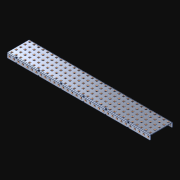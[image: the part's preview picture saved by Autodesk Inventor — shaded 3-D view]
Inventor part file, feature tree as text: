
AUTODESK INVENTOR PART (.ipt)
format: ipt  version: 2021 (Build 250183000, 183)  size: 2,406,400 bytes
history: native  units: in
note: dims shown in document units (in); Inventor stores cm internally (conversion verified against a paired STEP export)
features: extrude x225, other x225, sketch x4, pattern_linear x3
ambient origin geometry x8: Origin, YZ Plane, XZ Plane, XY Plane, X Axis, Y Axis, Z Axis, Center Point
bodies: Solid1 (feature_tree)
feature tree (457):
  pattern_linear  "Rectangular Pattern1"  Spacing1=0.182in  [1 undecoded]
  pattern_linear  "Rectangular Pattern2"  Spacing1=0.046in  [1 undecoded]
  pattern_linear  "Rectangular Pattern3"  Spacing1=0.5in  [1 undecoded]
  extrude  "Extrusion1"  Depth=0.046in
  sketch  "Sketch1"  dims[d0=0.182in]
  other  "Srf1"
  sketch  "Sketch2"  dims[d1=0.046in d2=0.0in]
  other  "Srf2"
  sketch  "Sketch3"  dims[d3=0.182in]
  other  "Srf3"
  other  "Srf4"
  other  "Srf5"
  other  "Srf6"
  other  "Srf7"
  other  "Srf8"
  other  "Srf9"
  other  "Srf10"
  other  "Srf11"
  other  "Srf12"
  other  "Srf13"
  other  "Srf14"
  other  "Srf15"
  other  "Srf16"
  other  "Srf17"
  other  "Srf18"
  other  "Srf19"
  other  "Srf20"
  other  "Srf21"
  other  "Srf22"
  other  "Srf23"
  other  "Srf24"
  other  "Srf25"
  other  "Srf26"
  other  "Srf27"
  other  "Srf28"
  other  "Srf29"
  other  "Srf30"
  other  "Srf31"
  other  "Srf32"
  other  "Srf33"
  other  "Srf34"
  other  "Srf38"
  other  "Srf39"
  other  "Srf40"
  other  "Srf41"
  other  "Srf42"
  other  "Srf43"
  other  "Srf44"
  other  "Srf45"
  other  "Srf46"
  other  "Srf47"
  other  "Srf48"
  other  "Srf49"
  other  "Srf50"
  other  "Srf51"
  other  "Srf52"
  other  "Srf53"
  other  "Srf54"
  other  "Srf55"
  other  "Srf56"
  other  "Srf57"
  other  "Srf58"
  other  "Srf59"
  other  "Srf60"
  other  "Srf61"
  other  "Srf62"
  other  "Srf63"
  other  "Srf64"
  other  "Srf65"
  other  "Srf66"
  other  "Srf67"
  other  "Srf68"
  other  "Srf72"
  other  "Srf73"
  other  "Srf74"
  other  "Srf75"
  other  "Srf76"
  other  "Srf77"
  other  "Srf78"
  other  "Srf79"
  other  "Srf80"
  other  "Srf81"
  other  "Srf82"
  other  "Srf83"
  other  "Srf84"
  other  "Srf85"
  other  "Srf86"
  other  "Srf87"
  other  "Srf88"
  other  "Srf89"
  other  "Srf90"
  other  "Srf91"
  other  "Srf92"
  other  "Srf93"
  other  "Srf94"
  other  "Srf95"
  other  "Srf96"
  other  "Srf97"
  other  "Srf98"
  other  "Srf99"
  other  "Srf100"
  other  "Srf101"
  other  "Srf102"
  other  "Srf103"
  other  "Srf107"
  other  "Srf108"
  other  "Srf109"
  other  "Srf110"
  other  "Srf111"
  other  "Srf112"
  other  "Srf113"
  other  "Srf114"
  other  "Srf115"
  other  "Srf116"
  other  "Srf117"
  other  "Srf118"
  other  "Srf119"
  other  "Srf120"
  other  "Srf121"
  other  "Srf122"
  other  "Srf123"
  other  "Srf124"
  other  "Srf125"
  other  "Srf126"
  other  "Srf127"
  other  "Srf128"
  other  "Srf129"
  other  "Srf130"
  other  "Srf131"
  other  "Srf132"
  other  "Srf133"
  other  "Srf134"
  other  "Srf135"
  other  "Srf136"
  other  "Srf137"
  other  "Srf138"
  other  "Srf142"
  other  "Srf143"
  other  "Srf144"
  other  "Srf145"
  other  "Srf146"
  other  "Srf147"
  other  "Srf148"
  other  "Srf149"
  other  "Srf150"
  other  "Srf151"
  other  "Srf152"
  other  "Srf153"
  other  "Srf154"
  other  "Srf155"
  other  "Srf156"
  other  "Srf157"
  other  "Srf158"
  other  "Srf159"
  other  "Srf160"
  other  "Srf161"
  other  "Srf162"
  other  "Srf163"
  other  "Srf164"
  other  "Srf165"
  other  "Srf166"
  other  "Srf167"
  other  "Srf168"
  other  "Srf169"
  other  "Srf170"
  other  "Srf171"
  other  "Srf172"
  other  "Srf173"
  other  "Srf177"
  other  "Srf178"
  other  "Srf179"
  other  "Srf180"
  other  "Srf181"
  other  "Srf182"
  other  "Srf183"
  other  "Srf184"
  other  "Srf185"
  other  "Srf186"
  other  "Srf187"
  other  "Srf188"
  other  "Srf189"
  other  "Srf190"
  other  "Srf191"
  other  "Srf192"
  other  "Srf193"
  other  "Srf194"
  other  "Srf195"
  other  "Srf196"
  other  "Srf197"
  other  "Srf198"
  other  "Srf199"
  other  "Srf200"
  other  "Srf201"
  other  "Srf202"
  other  "Srf203"
  other  "Srf204"
  other  "Srf205"
  other  "Srf206"
  other  "Srf207"
  other  "Srf208"
  other  "Srf212"
  other  "Srf213"
  other  "Srf214"
  other  "Srf215"
  other  "Srf216"
  other  "Srf217"
  other  "Srf218"
  other  "Srf219"
  other  "Srf220"
  other  "Srf221"
  other  "Srf222"
  other  "Srf223"
  other  "Srf224"
  other  "Srf225"
  other  "Srf226"
  other  "Srf227"
  other  "Srf228"
  other  "Srf229"
  other  "Srf230"
  other  "Srf231"
  other  "Srf232"
  other  "Srf233"
  other  "Srf234"
  other  "Srf235"
  other  "Srf236"
  other  "Srf237"
  other  "Srf238"
  other  "Srf239"
  other  "Srf240"
  other  "Srf241"
  other  "Srf242"
  sketch  "Sketch4"  dims[d4=0.046in d5=0.0in d6=0.182in d7=0.046in d8=0.0in d11=0.5in d12=12.5984in d14=0.5in d15=1.9685in d17=0.5in d18=12.5984in d20=0.5in d21=1.5in d22=0.0in]
  parser-record x1  (decoder bookkeeping rows leaked as tree rows — omitted from the tree; the rows remain in map.json)
  extrude  "ExtrusionSrf1"  Depth=0.046in
  extrude  "ExtrusionSrf2"  Depth=0.046in
  extrude  "ExtrusionSrf3"  Depth=0.046in
  extrude  "ExtrusionSrf4"  Depth=0.046in
  extrude  "ExtrusionSrf5"  Depth=0.046in
  extrude  "ExtrusionSrf6"  TaperAngle=0.0deg  [1 undecoded]
  extrude  "ExtrusionSrf7"  [1 undecoded]
  extrude  "ExtrusionSrf8"  [1 undecoded]
  extrude  "ExtrusionSrf9"  [1 undecoded]
  extrude  "ExtrusionSrf10"  [1 undecoded]
  extrude  "ExtrusionSrf11"  [1 undecoded]
  extrude  "ExtrusionSrf12"  [1 undecoded]
  extrude  "ExtrusionSrf13"  [1 undecoded]
  extrude  "ExtrusionSrf14"  [1 undecoded]
  extrude  "ExtrusionSrf15"  [1 undecoded]
  extrude  "ExtrusionSrf16"  [1 undecoded]
  extrude  "ExtrusionSrf17"  [1 undecoded]
  extrude  "ExtrusionSrf18"  [1 undecoded]
  extrude  "ExtrusionSrf19"  [1 undecoded]
  extrude  "ExtrusionSrf20"  [1 undecoded]
  extrude  "ExtrusionSrf21"  [1 undecoded]
  extrude  "ExtrusionSrf22"  [1 undecoded]
  extrude  "ExtrusionSrf23"  [1 undecoded]
  extrude  "ExtrusionSrf24"  [1 undecoded]
  extrude  "ExtrusionSrf25"  [1 undecoded]
  extrude  "ExtrusionSrf26"  [1 undecoded]
  extrude  "ExtrusionSrf27"  [1 undecoded]
  extrude  "ExtrusionSrf28"  [1 undecoded]
  extrude  "ExtrusionSrf29"  [1 undecoded]
  extrude  "ExtrusionSrf30"  [1 undecoded]
  extrude  "ExtrusionSrf31"  [1 undecoded]
  extrude  "ExtrusionSrf32"  [1 undecoded]
  extrude  "ExtrusionSrf33"  [1 undecoded]
  extrude  "ExtrusionSrf34"  [1 undecoded]
  extrude  "ExtrusionSrf38"  [1 undecoded]
  extrude  "ExtrusionSrf39"  [1 undecoded]
  extrude  "ExtrusionSrf40"  [1 undecoded]
  extrude  "ExtrusionSrf41"  [1 undecoded]
  extrude  "ExtrusionSrf42"  [1 undecoded]
  extrude  "ExtrusionSrf43"  [1 undecoded]
  extrude  "ExtrusionSrf44"  [1 undecoded]
  extrude  "ExtrusionSrf45"  [1 undecoded]
  extrude  "ExtrusionSrf46"  [1 undecoded]
  extrude  "ExtrusionSrf47"  [1 undecoded]
  extrude  "ExtrusionSrf48"  [1 undecoded]
  extrude  "ExtrusionSrf49"  [1 undecoded]
  extrude  "ExtrusionSrf50"  [1 undecoded]
  extrude  "ExtrusionSrf51"  [1 undecoded]
  extrude  "ExtrusionSrf52"  [1 undecoded]
  extrude  "ExtrusionSrf53"  [1 undecoded]
  extrude  "ExtrusionSrf54"  [1 undecoded]
  extrude  "ExtrusionSrf55"  [1 undecoded]
  extrude  "ExtrusionSrf56"  [1 undecoded]
  extrude  "ExtrusionSrf57"  [1 undecoded]
  extrude  "ExtrusionSrf58"  [1 undecoded]
  extrude  "ExtrusionSrf59"  [1 undecoded]
  extrude  "ExtrusionSrf60"  [1 undecoded]
  extrude  "ExtrusionSrf61"  [1 undecoded]
  extrude  "ExtrusionSrf62"  [1 undecoded]
  extrude  "ExtrusionSrf63"  [1 undecoded]
  extrude  "ExtrusionSrf64"  [1 undecoded]
  extrude  "ExtrusionSrf65"  [1 undecoded]
  extrude  "ExtrusionSrf66"  [1 undecoded]
  extrude  "ExtrusionSrf67"  [1 undecoded]
  extrude  "ExtrusionSrf68"  [1 undecoded]
  extrude  "ExtrusionSrf72"  [1 undecoded]
  extrude  "ExtrusionSrf73"  [1 undecoded]
  extrude  "ExtrusionSrf74"  [1 undecoded]
  extrude  "ExtrusionSrf75"  [1 undecoded]
  extrude  "ExtrusionSrf76"  [1 undecoded]
  extrude  "ExtrusionSrf77"  [1 undecoded]
  extrude  "ExtrusionSrf78"  [1 undecoded]
  extrude  "ExtrusionSrf79"  [1 undecoded]
  extrude  "ExtrusionSrf80"  [1 undecoded]
  extrude  "ExtrusionSrf81"  [1 undecoded]
  extrude  "ExtrusionSrf82"  [1 undecoded]
  extrude  "ExtrusionSrf83"  [1 undecoded]
  extrude  "ExtrusionSrf84"  [1 undecoded]
  extrude  "ExtrusionSrf85"  [1 undecoded]
  extrude  "ExtrusionSrf86"  [1 undecoded]
  extrude  "ExtrusionSrf87"  [1 undecoded]
  extrude  "ExtrusionSrf88"  [1 undecoded]
  extrude  "ExtrusionSrf89"  [1 undecoded]
  extrude  "ExtrusionSrf90"  [1 undecoded]
  extrude  "ExtrusionSrf91"  [1 undecoded]
  extrude  "ExtrusionSrf92"  [1 undecoded]
  extrude  "ExtrusionSrf93"  [1 undecoded]
  extrude  "ExtrusionSrf94"  [1 undecoded]
  extrude  "ExtrusionSrf95"  [1 undecoded]
  extrude  "ExtrusionSrf96"  [1 undecoded]
  extrude  "ExtrusionSrf97"  [1 undecoded]
  extrude  "ExtrusionSrf98"  [1 undecoded]
  extrude  "ExtrusionSrf99"  [1 undecoded]
  extrude  "ExtrusionSrf100"  [1 undecoded]
  extrude  "ExtrusionSrf101"  [1 undecoded]
  extrude  "ExtrusionSrf102"  [1 undecoded]
  extrude  "ExtrusionSrf103"  [1 undecoded]
  extrude  "ExtrusionSrf107"  [1 undecoded]
  extrude  "ExtrusionSrf108"  [1 undecoded]
  extrude  "ExtrusionSrf109"  [1 undecoded]
  extrude  "ExtrusionSrf110"  [1 undecoded]
  extrude  "ExtrusionSrf111"  [1 undecoded]
  extrude  "ExtrusionSrf112"  [1 undecoded]
  extrude  "ExtrusionSrf113"  [1 undecoded]
  extrude  "ExtrusionSrf114"  [1 undecoded]
  extrude  "ExtrusionSrf115"  [1 undecoded]
  extrude  "ExtrusionSrf116"  [1 undecoded]
  extrude  "ExtrusionSrf117"  [1 undecoded]
  extrude  "ExtrusionSrf118"  [1 undecoded]
  extrude  "ExtrusionSrf119"  [1 undecoded]
  extrude  "ExtrusionSrf120"  [1 undecoded]
  extrude  "ExtrusionSrf121"  [1 undecoded]
  extrude  "ExtrusionSrf122"  [1 undecoded]
  extrude  "ExtrusionSrf123"  [1 undecoded]
  extrude  "ExtrusionSrf124"  [1 undecoded]
  extrude  "ExtrusionSrf125"  [1 undecoded]
  extrude  "ExtrusionSrf126"  [1 undecoded]
  extrude  "ExtrusionSrf127"  [1 undecoded]
  extrude  "ExtrusionSrf128"  [1 undecoded]
  extrude  "ExtrusionSrf129"  [1 undecoded]
  extrude  "ExtrusionSrf130"  [1 undecoded]
  extrude  "ExtrusionSrf131"  [1 undecoded]
  extrude  "ExtrusionSrf132"  [1 undecoded]
  extrude  "ExtrusionSrf133"  [1 undecoded]
  extrude  "ExtrusionSrf134"  [1 undecoded]
  extrude  "ExtrusionSrf135"  [1 undecoded]
  extrude  "ExtrusionSrf136"  [1 undecoded]
  extrude  "ExtrusionSrf137"  [1 undecoded]
  extrude  "ExtrusionSrf138"  [1 undecoded]
  extrude  "ExtrusionSrf142"  [1 undecoded]
  extrude  "ExtrusionSrf143"  [1 undecoded]
  extrude  "ExtrusionSrf144"  [1 undecoded]
  extrude  "ExtrusionSrf145"  [1 undecoded]
  extrude  "ExtrusionSrf146"  [1 undecoded]
  extrude  "ExtrusionSrf147"  [1 undecoded]
  extrude  "ExtrusionSrf148"  [1 undecoded]
  extrude  "ExtrusionSrf149"  [1 undecoded]
  extrude  "ExtrusionSrf150"  [1 undecoded]
  extrude  "ExtrusionSrf151"  [1 undecoded]
  extrude  "ExtrusionSrf152"  [1 undecoded]
  extrude  "ExtrusionSrf153"  [1 undecoded]
  extrude  "ExtrusionSrf154"  [1 undecoded]
  extrude  "ExtrusionSrf155"  [1 undecoded]
  extrude  "ExtrusionSrf156"  [1 undecoded]
  extrude  "ExtrusionSrf157"  [1 undecoded]
  extrude  "ExtrusionSrf158"  [1 undecoded]
  extrude  "ExtrusionSrf159"  [1 undecoded]
  extrude  "ExtrusionSrf160"  [1 undecoded]
  extrude  "ExtrusionSrf161"  [1 undecoded]
  extrude  "ExtrusionSrf162"  [1 undecoded]
  extrude  "ExtrusionSrf163"  [1 undecoded]
  extrude  "ExtrusionSrf164"  [1 undecoded]
  extrude  "ExtrusionSrf165"  [1 undecoded]
  extrude  "ExtrusionSrf166"  [1 undecoded]
  extrude  "ExtrusionSrf167"  [1 undecoded]
  extrude  "ExtrusionSrf168"  [1 undecoded]
  extrude  "ExtrusionSrf169"  [1 undecoded]
  extrude  "ExtrusionSrf170"  [1 undecoded]
  extrude  "ExtrusionSrf171"  [1 undecoded]
  extrude  "ExtrusionSrf172"  [1 undecoded]
  extrude  "ExtrusionSrf173"  [1 undecoded]
  extrude  "ExtrusionSrf177"  [1 undecoded]
  extrude  "ExtrusionSrf178"  [1 undecoded]
  extrude  "ExtrusionSrf179"  [1 undecoded]
  extrude  "ExtrusionSrf180"  [1 undecoded]
  extrude  "ExtrusionSrf181"  [1 undecoded]
  extrude  "ExtrusionSrf182"  [1 undecoded]
  extrude  "ExtrusionSrf183"  [1 undecoded]
  extrude  "ExtrusionSrf184"  [1 undecoded]
  extrude  "ExtrusionSrf185"  [1 undecoded]
  extrude  "ExtrusionSrf186"  [1 undecoded]
  extrude  "ExtrusionSrf187"  [1 undecoded]
  extrude  "ExtrusionSrf188"  [1 undecoded]
  extrude  "ExtrusionSrf189"  [1 undecoded]
  extrude  "ExtrusionSrf190"  [1 undecoded]
  extrude  "ExtrusionSrf191"  [1 undecoded]
  extrude  "ExtrusionSrf192"  [1 undecoded]
  extrude  "ExtrusionSrf193"  [1 undecoded]
  extrude  "ExtrusionSrf194"  [1 undecoded]
  extrude  "ExtrusionSrf195"  [1 undecoded]
  extrude  "ExtrusionSrf196"  [1 undecoded]
  extrude  "ExtrusionSrf197"  [1 undecoded]
  extrude  "ExtrusionSrf198"  [1 undecoded]
  extrude  "ExtrusionSrf199"  [1 undecoded]
  extrude  "ExtrusionSrf200"  [1 undecoded]
  extrude  "ExtrusionSrf201"  [1 undecoded]
  extrude  "ExtrusionSrf202"  [1 undecoded]
  extrude  "ExtrusionSrf203"  [1 undecoded]
  extrude  "ExtrusionSrf204"  [1 undecoded]
  extrude  "ExtrusionSrf205"  [1 undecoded]
  extrude  "ExtrusionSrf206"  [1 undecoded]
  extrude  "ExtrusionSrf207"  [1 undecoded]
  extrude  "ExtrusionSrf208"  [1 undecoded]
  extrude  "ExtrusionSrf212"  [1 undecoded]
  extrude  "ExtrusionSrf213"  [1 undecoded]
  extrude  "ExtrusionSrf214"  [1 undecoded]
  extrude  "ExtrusionSrf215"  [1 undecoded]
  extrude  "ExtrusionSrf216"  [1 undecoded]
  extrude  "ExtrusionSrf217"  [1 undecoded]
  extrude  "ExtrusionSrf218"  [1 undecoded]
  extrude  "ExtrusionSrf219"  [1 undecoded]
  extrude  "ExtrusionSrf220"  [1 undecoded]
  extrude  "ExtrusionSrf221"  [1 undecoded]
  extrude  "ExtrusionSrf222"  [1 undecoded]
  extrude  "ExtrusionSrf223"  [1 undecoded]
  extrude  "ExtrusionSrf224"  [1 undecoded]
  extrude  "ExtrusionSrf225"  [1 undecoded]
  extrude  "ExtrusionSrf226"  [1 undecoded]
  extrude  "ExtrusionSrf227"  [1 undecoded]
  extrude  "ExtrusionSrf228"  [1 undecoded]
  extrude  "ExtrusionSrf229"  [1 undecoded]
  extrude  "ExtrusionSrf230"  [1 undecoded]
  extrude  "ExtrusionSrf231"  [1 undecoded]
  extrude  "ExtrusionSrf232"  [1 undecoded]
  extrude  "ExtrusionSrf233"  [1 undecoded]
  extrude  "ExtrusionSrf234"  [1 undecoded]
  extrude  "ExtrusionSrf235"  [1 undecoded]
  extrude  "ExtrusionSrf236"  [1 undecoded]
  extrude  "ExtrusionSrf237"  [1 undecoded]
  extrude  "ExtrusionSrf238"  [1 undecoded]
  extrude  "ExtrusionSrf239"  [1 undecoded]
  extrude  "ExtrusionSrf240"  [1 undecoded]
  extrude  "ExtrusionSrf241"  [1 undecoded]
  extrude  "ExtrusionSrf242"  [1 undecoded]
note: 222 required parameter values undecoded (feature->parameter linkage not recoverable at this tier; creation-order binding heuristic only, values carry confidence <= 0.55)
